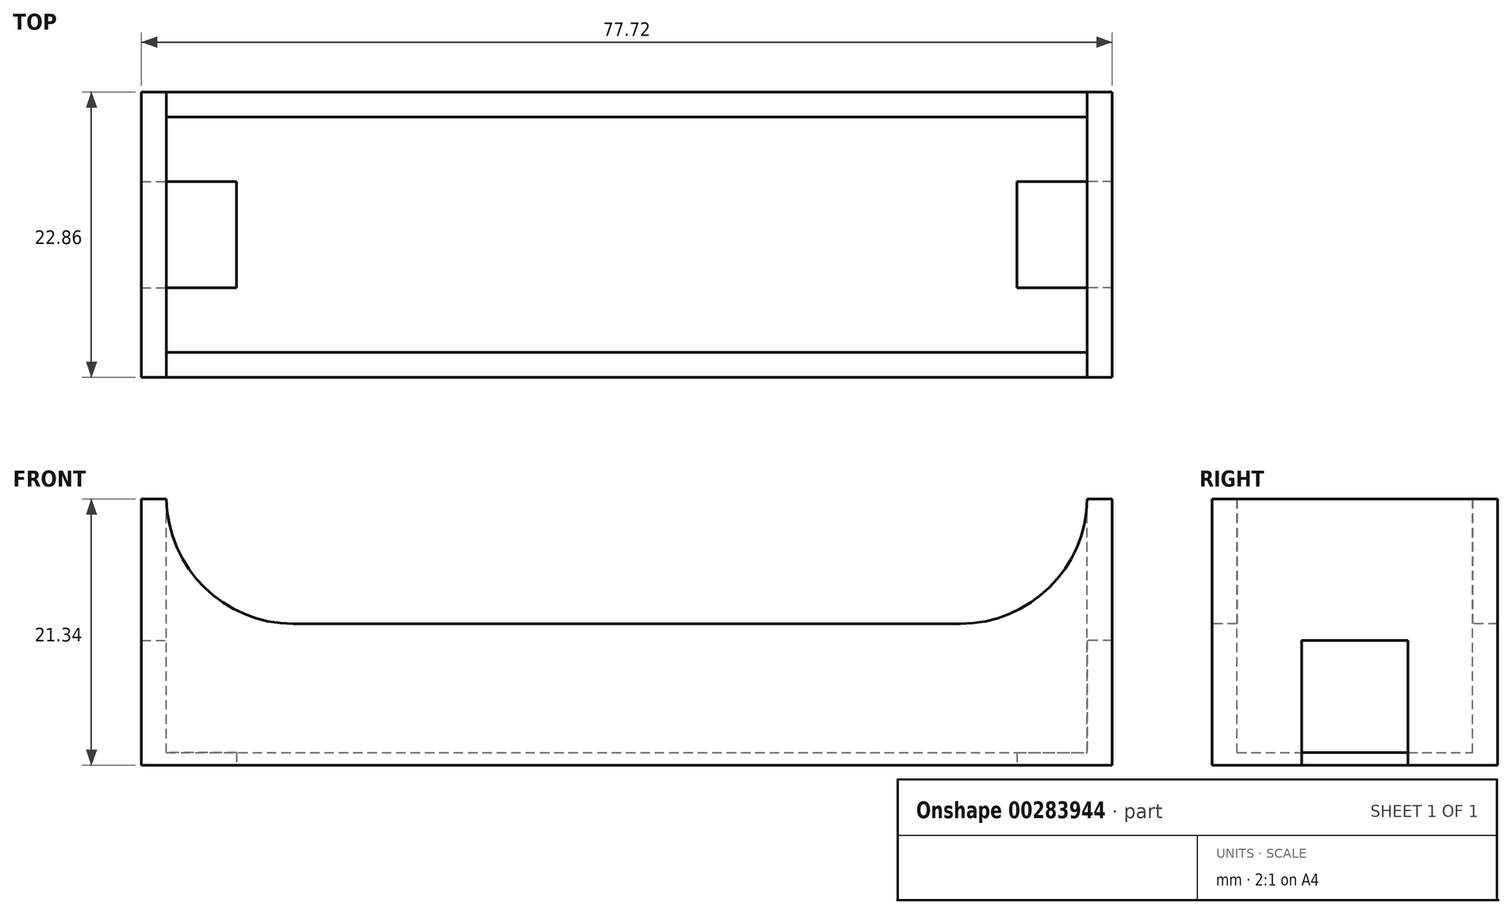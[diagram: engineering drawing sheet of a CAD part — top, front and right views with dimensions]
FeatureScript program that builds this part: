
annotation { "Feature Type Name" : "Feature", "Feature Type Description" : "" }
export const myFeature = defineFeature(function(context is Context, id is Id, definition is map)
    precondition{}
    {
        {
            var Q0;
            Q0=qCreatedBy(makeId("Top.planeOp"),FACE);
            var sketch = newSketch(context, id + "F0", { "sketchPlane" : qUnion([Q0])});
            skLineSegment(sketch, "E0.bottom", {"start": v(0, 0) * mm, "end": v(77.72, 0) * mm});
            skLineSegment(sketch, "E0.top", {"start": v(0, 22.86) * mm, "end": v(77.72, 22.86) * mm});
            skLineSegment(sketch, "E0.left", {"start": v(0, 0) * mm, "end": v(0, 22.86) * mm});
            skLineSegment(sketch, "E0.right", {"start": v(77.72, 0) * mm, "end": v(77.72, 22.86) * mm});
            skSolve(sketch);
        }
        {
            var Q0;
            Q0 = qSketchRegion(id + "F0", true);
            extrude(context, id + "F1", {"entities" : qUnion([Q0]), "depth" : 21.34 * mm});
        }
        {
            var Q0;
            Q0=makeQuery(id+"F1.opExtrude","CAP_FACE",FACE,{"disambiguationData":[OSD([sQuery(id+"F0.wireOp",EDGE,"E0.bottom"),sQuery(id+"F0.wireOp",EDGE,"E0.top"),sQuery(id+"F0.wireOp",EDGE,"E0.left"),sQuery(id+"F0.wireOp",EDGE,"E0.right")])],"isStart":false});
            var sketch = newSketch(context, id + "F2", { "sketchPlane" : qUnion([Q0])});
            skLineSegment(sketch, "E1.bottom", {"start": v(2, 2) * mm, "end": v(75.72, 2) * mm});
            skLineSegment(sketch, "E1.top", {"start": v(2, 20.86) * mm, "end": v(75.72, 20.86) * mm});
            skLineSegment(sketch, "E1.left", {"start": v(2, 2) * mm, "end": v(2, 20.86) * mm});
            skLineSegment(sketch, "E1.right", {"start": v(75.72, 2) * mm, "end": v(75.72, 20.86) * mm});
            skSolve(sketch);
        }
        {
            var Q0;
            Q0 = qSketchRegion(id + "F2", true);
            extrude(context, id + "F3", {"entities" : qUnion([Q0]), "operationType" : NewBodyOperationType.REMOVE, "oppositeDirection" : true, "depth" : 20.32 * mm});
        }
        {
            var Q0;
            Q0=makeQuery(id+"F1.opExtrude","CAP_FACE",FACE,{"disambiguationData":[OSD([sQuery(id+"F0.wireOp",EDGE,"E0.bottom"),sQuery(id+"F0.wireOp",EDGE,"E0.top"),sQuery(id+"F0.wireOp",EDGE,"E0.left"),sQuery(id+"F0.wireOp",EDGE,"E0.right")])],"isStart":true});
            var sketch = newSketch(context, id + "F4", { "sketchPlane" : qUnion([Q0])});
            skPoint(sketch, "E2", {"position": v(0, -11.43) * mm});
            skLineSegment(sketch, "E3.bottom", {"start": v(0, -15.68) * mm, "end": v(7.62, -15.68) * mm});
            skLineSegment(sketch, "E3.top", {"start": v(0, -7.18) * mm, "end": v(7.62, -7.18) * mm});
            skLineSegment(sketch, "E3.left", {"start": v(0, -15.68) * mm, "end": v(0, -7.18) * mm});
            skLineSegment(sketch, "E3.right", {"start": v(7.62, -15.68) * mm, "end": v(7.62, -7.18) * mm});
            skLineSegment(sketch, "E4", {"start": v(38.86, -22.86) * mm, "end": v(38.86, 0) * mm, "construction": true});
            skPoint(sketch, "E5.MirrorP", {"position": v(77.72, -11.43) * mm});
            skLineSegment(sketch, "E6.MirrorCS", {"start": v(70.1, -15.68) * mm, "end": v(70.1, -7.18) * mm});
            skLineSegment(sketch, "E7.MirrorCS", {"start": v(77.72, -15.68) * mm, "end": v(77.72, -7.18) * mm});
            skLineSegment(sketch, "E8.MirrorCS", {"start": v(77.72, -7.18) * mm, "end": v(70.1, -7.18) * mm});
            skLineSegment(sketch, "E9.MirrorCS", {"start": v(77.72, -15.68) * mm, "end": v(70.1, -15.68) * mm});
            skSolve(sketch);
        }
        {
            var Q0;
            Q0 = qSketchRegion(id + "F4", true);
            extrude(context, id + "F5", {"entities" : qUnion([Q0]), "operationType" : NewBodyOperationType.REMOVE, "oppositeDirection" : true, "depth" : 10 * mm});
        }
        {
            var Q0;
            Q0=qCreatedBy(makeId("Front.planeOp"),FACE);
            var sketch = newSketch(context, id + "F6", { "sketchPlane" : qUnion([Q0])});
            skLineSegment(sketch, "E10.bottom", {"start": v(2, 21.34) * mm, "end": v(75.72, 21.34) * mm});
            skLineSegment(sketch, "E10.top", {"start": v(2, 11.34) * mm, "end": v(75.72, 11.34) * mm});
            skLineSegment(sketch, "E10.left", {"start": v(2, 21.34) * mm, "end": v(2, 11.34) * mm});
            skLineSegment(sketch, "E10.right", {"start": v(75.72, 21.34) * mm, "end": v(75.72, 11.34) * mm});
            skSolve(sketch);
        }
        {
            var Q0;
            Q0 = qSketchRegion(id + "F6", true);
            extrude(context, id + "F7", {"entities" : qUnion([Q0]), "operationType" : NewBodyOperationType.REMOVE, "oppositeDirection" : true, "depth" : 25 * mm, "hasSecondDirection" : true, "secondDirectionOppositeDirection" : false, "secondDirectionDepth" : 25 * mm});
        }
        {
            var Q0;
            {var subQ0=sQuery(id+"F6.wireOp",EDGE,"E10.top");var subQ1=sQuery(id+"F6.wireOp",EDGE,"E10.left");Q0=makeQuery(id+"F7.boolean.opBoolean","COPY",EDGE,{"disambiguationData":[TD([makeQuery(id+"F1.opExtrude","SWEPT_FACE",FACE,{"disambiguationData":[OSD([sQuery(id+"F0.wireOp",EDGE,"E0.bottom")])]})])],"derivedFrom":makeQuery(id+"F7.opExtrude","SWEPT_EDGE",EDGE,{"disambiguationData":[OSD([subQ0,subQ1])]})});}
            var Q1;
            {var subQ0=sQuery(id+"F6.wireOp",EDGE,"E10.top");var subQ1=sQuery(id+"F6.wireOp",EDGE,"E10.left");Q1=makeQuery(id+"F7.boolean.opBoolean","COPY",EDGE,{"disambiguationData":[TD([makeQuery(id+"F1.opExtrude","SWEPT_FACE",FACE,{"disambiguationData":[OSD([sQuery(id+"F0.wireOp",EDGE,"E0.top")])]})])],"derivedFrom":makeQuery(id+"F7.opExtrude","SWEPT_EDGE",EDGE,{"disambiguationData":[OSD([subQ0,subQ1])]})});}
            var Q2;
            {var subQ0=sQuery(id+"F6.wireOp",EDGE,"E10.top");var subQ1=sQuery(id+"F6.wireOp",EDGE,"E10.right");Q2=makeQuery(id+"F7.boolean.opBoolean","COPY",EDGE,{"disambiguationData":[TD([makeQuery(id+"F1.opExtrude","SWEPT_FACE",FACE,{"disambiguationData":[OSD([sQuery(id+"F0.wireOp",EDGE,"E0.bottom")])]})])],"derivedFrom":makeQuery(id+"F7.opExtrude","SWEPT_EDGE",EDGE,{"disambiguationData":[OSD([subQ0,subQ1])]})});}
            var Q3;
            {var subQ0=sQuery(id+"F6.wireOp",EDGE,"E10.top");var subQ1=sQuery(id+"F6.wireOp",EDGE,"E10.right");Q3=makeQuery(id+"F7.boolean.opBoolean","COPY",EDGE,{"disambiguationData":[TD([makeQuery(id+"F1.opExtrude","SWEPT_FACE",FACE,{"disambiguationData":[OSD([sQuery(id+"F0.wireOp",EDGE,"E0.top")])]})])],"derivedFrom":makeQuery(id+"F7.opExtrude","SWEPT_EDGE",EDGE,{"disambiguationData":[OSD([subQ0,subQ1])]})});}
            fillet(context, id + "F8", {"entities" : qUnion([Q0, Q1, Q2, Q3]), "radius" : 10.16 * mm, "tangentPropagation" : true, "allowEdgeOverflow" : false});
        }
    });
